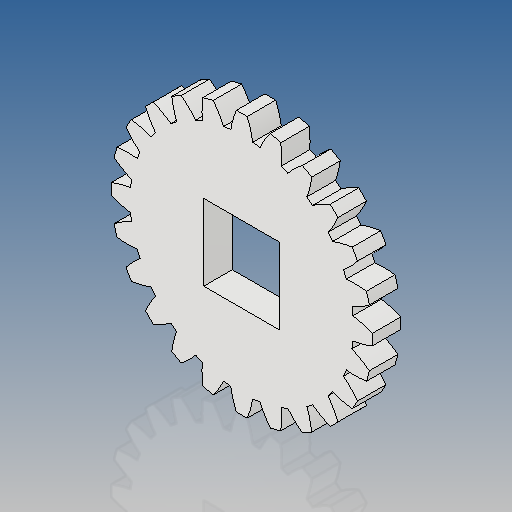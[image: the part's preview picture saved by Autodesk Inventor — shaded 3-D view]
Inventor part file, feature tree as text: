
AUTODESK INVENTOR PART (.ipt)
format: ipt  version: 2017 (Build 210142000, 142)  size: 232,960 bytes
history: native  units: mm
features: other x6, extrude x1, sketch x1, reference x1
ambient origin geometry x8: Origin, YZ Plane, XZ Plane, XY Plane, X Axis, Y Axis, Z Axis, Center Point
bodies: Body1 (feature_tree)
feature tree (9):
  other  "Sólido1"
  extrude  "Extrusión1"  Depth=6.0mm TaperAngle=0.0deg
  other  "Dientes de engranaje recto1"
  sketch  "Boceto1"  dims[d0=55.0mm d1=6.0mm d2=0.0mm]
  reference  "Referencia1"
  other  "iFeature1:1"
  other  "<userpath>\Dropbox\E\Caja Motriz\transmision Engranajes\Polea Compuesta.iam"
  other  "Polea Compuesta.iam"
  other  "dado polea:1"
